# Revit family: Lighting-UrbanLighting-GEWISS-ELIA-OL-LED_APPLIQUE_WALLMOUNTED
name_source: partatom
category: Apparecchi per illuminazione
units: mm (PartAtom-declared; Revit-internal decimal feet)

## family parameters
Condiviso = No
Host = Superficie
Punto di calcolo locali = Sì
Quota connettore circolare = Usa diametro
Sorgente d'illuminazione = Sì
Taglio con vuoti quando caricato = No
Tipo di parte = Normale

## types (6) — shared parameters
Angolo inclinazione = 60.00°
Application = External
Body = Die-cast aluminium -
Catalogue = LIGHTING
Classification: = -
Color Rendering Index = CRI>80
Colour : = -
Context = Outdoor architectural lighting
Control System = Stand alone
DIN 18032-3 certification = -
Device with reduced surface temperature = -
Driver = Included
Driver Box = Built-in
Driver failure rate = F025 = 50.000h Tq 25°C
Electrocod = 2419
Eletrical and lighting features = -
Emetti da lunghezza linea = 610 mm
External screw = -
File diagramma fotometrico = generic
Filtro dei colori = 16777215
Fixing = Stainless steel support
Gasket = -
General information = -
Glow Wire Test : = 750 °C
IDF = 3b6412d1-6c2a-4f9d-8ab7-e3409a0bd29e
IDT = 30b4c0cd-5e0e-4ed9-a176-a58e6e2db9cb
IP degree = IP65
IPEA = -
Immagine tipo = EliaOL.jpg
Installationa and maintenance = -
Insulation class = I
LED Maintenance = Not available
Lifetime = L80B50 (Tq25°C) = 50.000h
Locking Hook = -
Lugnezza massima = 20 mm  [stored 0.0656168 ft]
Luminaire = LED luminaire for diffuse light
Materials = -
Maximum surface exposed to the wind : = -
Mouting and installation = Wall mounting
Operating temperature : = -20° +45°
Optic = Wide opal
Optic : = -
Optic Maintenance = Not available
Optic and illuminating features = -
Overvoltage protection = DM 0,5KV / CM 1KV
POSIZIONE = 80000
Photobiological Risk Class = RG0
Produttore = GEWISS S.p.A.
Prospetto di default = 1219 mm
Rated frequency (Hz) = 50/60 Hz
Shield type = Polycarbonate
Shock resistance = IK08
Standard Deviation Colour Matching = SDCM = 5
Standard- = -
Standards and approvals = -
Stocking temperature = -20° +65°
Supply voltage = 100-240 V
Technical sheet = https://www.gewiss.com
Tilt- = -
Type of light source = LED - Not replaceable
URL = https://www.gewiss.com
Unified Glare Rating = UGR < 25
Unique digital code (Datamatrix) = Currently not present
Variazione temperatura colore lampada con luminosità attenuata = <Nessuno>
Version file RFA = 21.4
Warranty = 5 years
Wiring = With connection terminal
larghezza lampada = -4 mm

## per-type parameters (varying)
| type | Colour | Descrizione | EAN code | Modello | Versions |
| GWF2110FR857 - ELIA OL ST AL ON/OFF 5700K WHITE | White | ELIA OL ST AL ON/OFF 5700K WHITE | 8034035077364 | GWF2110FR857 | Standard White |
| GWF2100FR840 - ELIA OL ST AL ON/OFF 4000K BLACK | Black | ELIA OL ST AL ON/OFF 4000K BLACK | 8034035077326 | GWF2100FR840 | Standard Black |
| GWF2100FR857 - ELIA OL ST AL ON/OFF 5700K BLACK | Black | ELIA OL ST AL ON/OFF 5700K BLACK | 8034035077333 | GWF2100FR857 | Standard Black |
| GWF2110FR830 - ELIA OL ST AL ON/OFF 3000K WHITE | White | ELIA OL ST AL ON/OFF 3000K WHITE | 8034035077340 | GWF2110FR830 | Standard White |
| GWF2100FR830 - ELIA OL ST AL ON/OFF 3000K BLACK | Black | ELIA OL ST AL ON/OFF 3000K BLACK | 8034035077319 | GWF2100FR830 | Standard Black |
| GWF2110FR840 - ELIA OL ST AL ON/OFF 4000K WHITE | White | ELIA OL ST AL ON/OFF 4000K WHITE | 8034035077357 | GWF2110FR840 | Standard White |

note: [stored X ft] marks values corroborated as IEEE doubles in the binary element streams (Revit-internal decimal feet)
